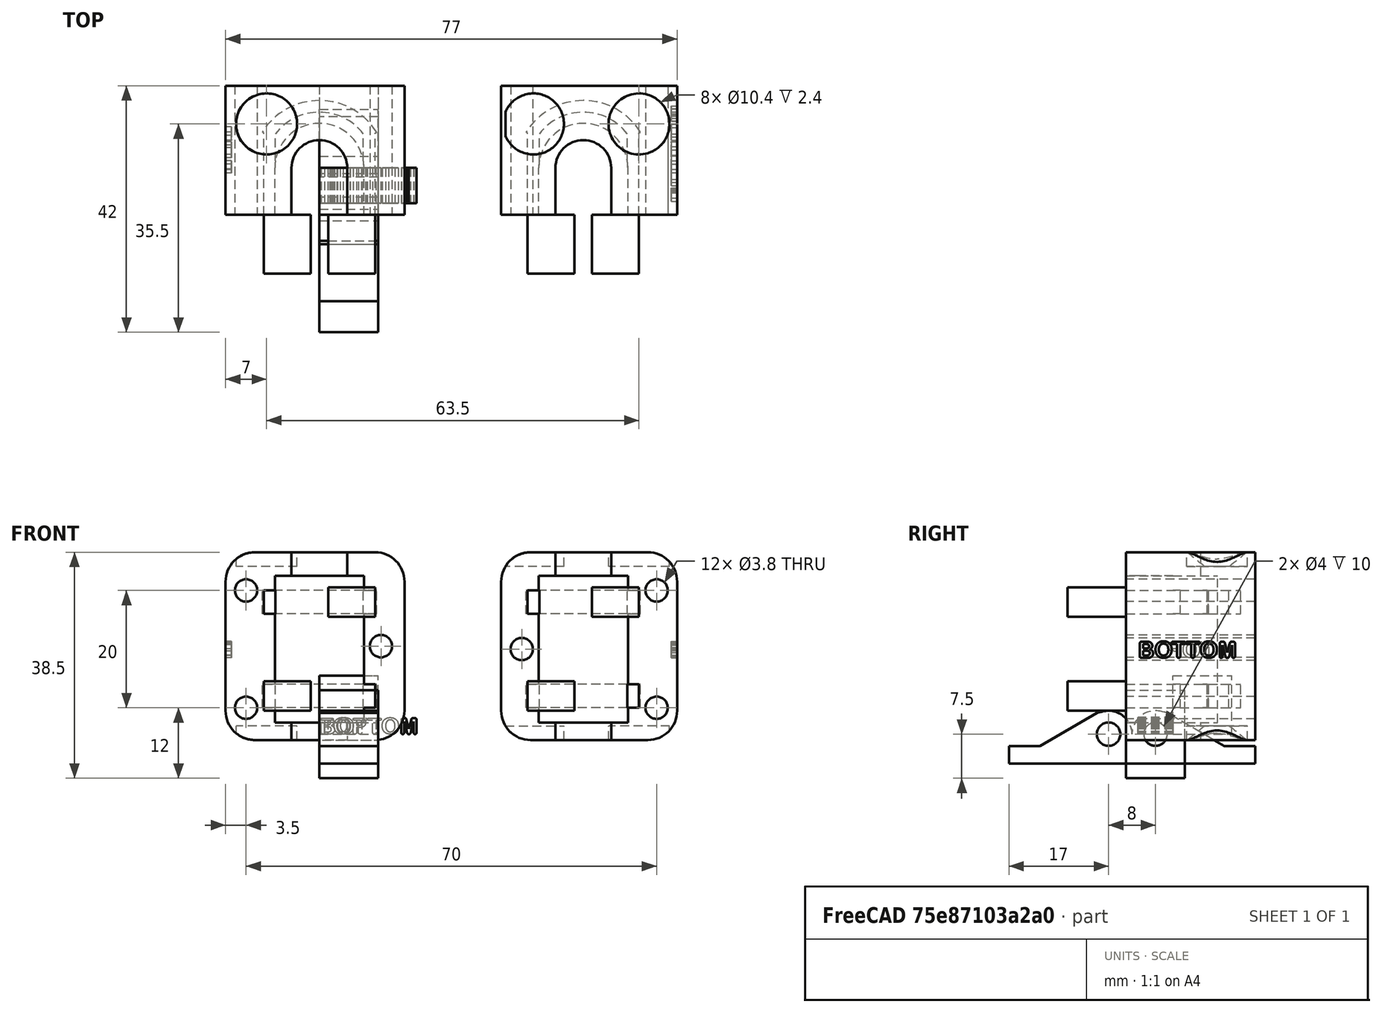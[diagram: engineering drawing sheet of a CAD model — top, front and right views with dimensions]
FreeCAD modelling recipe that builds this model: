
FCSTD DOCUMENT  (FreeCAD 0.16R6712 (Git))
Label: ParkingNozzleSlider
License: All rights reserved
LicenseURL: http://en.wikipedia.org/wiki/All_rights_reserved
objects: Part::Cylinder×51, Part::Box×26, Part::MultiFuse×26, Part::Cut×17, Part::Feature×3, Part::Part2DObjectPython×2, Part::Extrusion×2
note: 127 computed .brp shape members not serialized (recipe doc carries the construction recipe); baked Part::Feature solids carry a one-line shape summary decoded from their .brp

FEATURE [Part::Box] Box  label="Würfel"
  Height = 10
  Length = 10
  Width = 10
FEATURE [Part::Cylinder] Cylinder001  label="RJ4JP"
  Angle = 360
  Height = 25
  Placement = pos=(0,0,-0.5) rot=(0,0,1;0rad)
  Radius = 7.6
FEATURE [Part::Cylinder] Cylinder002  label="LinearStange8mm"
  Angle = 360
  Height = 44
  Placement = pos=(0,0,-10) rot=(0,0,1;0rad)
  Radius = 4.5
FEATURE [Part::Cylinder] Cylinder003  label="LinearSpacer9mm"
  Angle = 360
  Height = 34
  Placement = pos=(0,0,-5) rot=(0,0,1;0rad)
  Radius = 4.75
FEATURE [Part::MultiFuse] Fusion  label="GleitlagerAusspahrung"
  Shapes = -> [Cylinder001,Cylinder003,Cylinder002]
FEATURE [Part::Cylinder] Cylinder004  label="Zylinder001"
  Angle = 116
  Height = 4
  Placement = pos=(0,0,0) rot=(0,0,1;0.558505rad)
  Radius = 11.5
FEATURE [Part::Cylinder] Cylinder005  label="Zylinder002"
  Angle = 116
  Height = 4
  Placement = pos=(0,0,0) rot=(0,0,1;0.558505rad)
  Radius = 9.5
FEATURE [Part::Cut] Cut
  Base = -> Cylinder004
  Tool = -> Cylinder005
FEATURE [Part::Box] Box001  label="Würfel001"
  Height = 4
  Length = 2
  Placement = pos=(-9.5,-11,0) rot=(0,0,1;0rad)
  Width = 17
FEATURE [Part::Box] Box002  label="Würfel002"
  Height = 4
  Length = 2
  Placement = pos=(7.5,-11,0) rot=(0,0,1;0rad)
  Width = 17
FEATURE [Part::MultiFuse] Fusion001  label="KabelbinderAusspahrung002"
  Placement = pos=(0,0,18) rot=(0,0,1;0rad)
  Shapes = -> [Cut,Box002,Box001]
FEATURE [Part::Box] Box009  label="Würfel009"
  Height = 15
  Length = 10
  Placement = pos=(0,-8,-7.5) rot=(0,0,1;0rad)
  Width = 10
FEATURE [Part::Cylinder] Cylinder014  label="Zylinder008"
  Angle = 116
  Height = 4
  Placement = pos=(0,0,0) rot=(0,0,1;0.558505rad)
  Radius = 11.5
FEATURE [Part::Cylinder] Cylinder015  label="Zylinder009"
  Angle = 116
  Height = 4
  Placement = pos=(0,0,0) rot=(0,0,1;0.558505rad)
  Radius = 9.5
FEATURE [Part::Cut] Cut004
  Base = -> Cylinder014
  Tool = -> Cylinder015
FEATURE [Part::Box] Box010  label="Würfel010"
  Height = 4
  Length = 2
  Placement = pos=(-9.5,-11,0) rot=(0,0,1;0rad)
  Width = 17
FEATURE [Part::Box] Box011  label="Würfel011"
  Height = 4
  Length = 2
  Placement = pos=(7.5,-11,0) rot=(0,0,1;0rad)
  Width = 17
FEATURE [Part::MultiFuse] Fusion008  label="KabelbinderAusspahrung005"
  Placement = pos=(0,0,2) rot=(0,0,1;0rad)
  Shapes = -> [Cut004,Box011,Box010]
FEATURE [Part::Box] Box016  label="Block_A"
  Height = 32
  Length = 30.5
  Placement = pos=(-16,-8,-1) rot=(0,0,1;0rad)
  Width = 22
FEATURE [Part::Box] Box017  label="Würfel017"
  Height = 44
  Length = 9.5
  Placement = pos=(-4.75,-11,-10) rot=(0,0,1;0rad)
  Width = 11
FEATURE [Part::Box] Box018  label="Würfel018"
  Height = 25
  Length = 15.2
  Placement = pos=(-7.6,-11,-0.5) rot=(0,0,1;0rad)
  Width = 11
FEATURE [Part::MultiFuse] Fusion014  label="Schacht"
  Shapes = -> [Box017,Box018]
FEATURE [Part::MultiFuse] Fusion015  label="RJ4JP_Cut_Full_A"
  Shapes = -> [Fusion,Fusion001,Fusion008,Fusion014]
FEATURE [Part::Cylinder] Cylinder016  label="RJ4JP001"
  Angle = 360
  Height = 25
  Placement = pos=(0,0,-0.5) rot=(0,0,1;0rad)
  Radius = 7.6
FEATURE [Part::Cylinder] Cylinder017  label="LinearStange8mm001"
  Angle = 360
  Height = 44
  Placement = pos=(0,0,-10) rot=(0,0,1;0rad)
  Radius = 4.5
FEATURE [Part::Cylinder] Cylinder018  label="LinearSpacer9mm001"
  Angle = 360
  Height = 34
  Placement = pos=(0,0,-5) rot=(0,0,1;0rad)
  Radius = 4.75
FEATURE [Part::MultiFuse] Fusion016  label="GleitlagerAusspahrung001"
  Shapes = -> [Cylinder016,Cylinder018,Cylinder017]
FEATURE [Part::Cylinder] Cylinder019  label="Zylinder010"
  Angle = 116
  Height = 4
  Placement = pos=(0,0,0) rot=(0,0,1;0.558505rad)
  Radius = 11.5
FEATURE [Part::Cylinder] Cylinder020  label="Zylinder011"
  Angle = 116
  Height = 4
  Placement = pos=(0,0,0) rot=(0,0,1;0.558505rad)
  Radius = 9.5
FEATURE [Part::Cut] Cut005
  Base = -> Cylinder019
  Tool = -> Cylinder020
FEATURE [Part::Box] Box019  label="Würfel019"
  Height = 4
  Length = 2
  Placement = pos=(-9.5,-11,0) rot=(0,0,1;0rad)
  Width = 17
FEATURE [Part::Box] Box020  label="Würfel020"
  Height = 4
  Length = 2
  Placement = pos=(7.5,-11,0) rot=(0,0,1;0rad)
  Width = 17
FEATURE [Part::MultiFuse] Fusion017  label="KabelbinderAusspahrung006"
  Placement = pos=(0,0,18) rot=(0,0,1;0rad)
  Shapes = -> [Cut005,Box020,Box019]
FEATURE [Part::Cylinder] Cylinder021  label="Zylinder012"
  Angle = 116
  Height = 4
  Placement = pos=(0,0,0) rot=(0,0,1;0.558505rad)
  Radius = 11.5
FEATURE [Part::Cylinder] Cylinder022  label="Zylinder013"
  Angle = 116
  Height = 4
  Placement = pos=(0,0,0) rot=(0,0,1;0.558505rad)
  Radius = 9.5
FEATURE [Part::Cut] Cut006
  Base = -> Cylinder021
  Tool = -> Cylinder022
FEATURE [Part::Box] Box021  label="Würfel021"
  Height = 4
  Length = 2
  Placement = pos=(-9.5,-11,0) rot=(0,0,1;0rad)
  Width = 17
FEATURE [Part::Box] Box022  label="Würfel022"
  Height = 4
  Length = 2
  Placement = pos=(7.5,-11,0) rot=(0,0,1;0rad)
  Width = 17
FEATURE [Part::MultiFuse] Fusion018  label="KabelbinderAusspahrung007"
  Placement = pos=(0,0,2) rot=(0,0,1;0rad)
  Shapes = -> [Cut006,Box022,Box021]
FEATURE [Part::Box] Box023  label="Würfel023"
  Height = 44
  Length = 9.5
  Placement = pos=(-4.75,-11,-10) rot=(0,0,1;0rad)
  Width = 11
FEATURE [Part::Box] Box024  label="Würfel024"
  Height = 25
  Length = 15.2
  Placement = pos=(-7.6,-11,-0.5) rot=(0,0,1;0rad)
  Width = 11
FEATURE [Part::MultiFuse] Fusion019  label="Schacht001"
  Shapes = -> [Box023,Box024]
FEATURE [Part::MultiFuse] Fusion020  label="RJ4JP_Cut_Full_B"
  Placement = pos=(45,0,0) rot=(0,0,1;0rad)
  Shapes = -> [Fusion016,Fusion017,Fusion018,Fusion019]
FEATURE [Part::MultiFuse] Fusion021  label="X_RJ4JP_Cut"
  Placement = pos=(0,0,2.5) rot=(0,0,1;0rad)
  Shapes = -> [Fusion015,Fusion020]
FEATURE [Part::Box] Box025  label="Block_B"
  Height = 32
  Length = 30
  Placement = pos=(31,-8,-1) rot=(0,0,1;0rad)
  Width = 22
FEATURE [Part::MultiFuse] Fusion022  label="GleitBlock"
  Shapes = -> [Box016,Box025]
FEATURE [Part::Cut] Cut007  label="GleitBloecke"
  Base = -> Fusion022
  Tool = -> Fusion021
FEATURE [Part::Cylinder] Cylinder025  label="Zylinder016"
  Angle = 360
  Height = 10
  Radius = 2
FEATURE [Part::Cylinder] Cylinder026  label="Zylinder017"
  Angle = 360
  Height = 10
  Radius = 4
FEATURE [Part::Cut] Cut009
  Base = -> Cylinder026
  Placement = pos=(0,-11,0) rot=(0,0,1;0rad)
  Tool = -> Cylinder025
FEATURE [Part::Box] Box028  label="Würfel027"
  Height = 10
  Length = 3
  Placement = pos=(2,-28,0) rot=(0,0,1;0rad)
  Width = 22
FEATURE [Part::Box] Box029  label="Würfel028"
  Height = 10
  Length = 1
  Placement = pos=(3.9,-26,0) rot=(0,0,1;0.523599rad)
  Width = 15
FEATURE [Part::Box] Box030  label="Würfel029"
  Height = 10
  Length = 3.3
  Placement = pos=(2,-21.5,0) rot=(0,0,1;0.523599rad)
  Width = 8
FEATURE [Part::Cylinder] Cylinder027  label="Zylinder018"
  Angle = 360
  Height = 10
  Placement = pos=(2,-15,0) rot=(0,0,1;0rad)
  Radius = 2
FEATURE [Part::Cylinder] Cylinder028  label="Zylinder019"
  Angle = 360
  Height = 10
  Placement = pos=(-2.73,-12.5,0) rot=(0,0,1;0rad)
  Radius = 1
FEATURE [Part::MultiFuse] Fusion023
  Shapes = -> [Cut009,Cylinder027,Cylinder028,Box028,Box029,Box030]
FEATURE [Part::Cylinder] Cylinder029  label="Zylinder020"
  Angle = 360
  Height = 10
  Radius = 2
FEATURE [Part::Cylinder] Cylinder030  label="Zylinder021"
  Angle = 360
  Height = 10
  Radius = 4
FEATURE [Part::Cut] Cut010
  Base = -> Cylinder030
  Placement = pos=(0,-11,0) rot=(0,0,1;0rad)
  Tool = -> Cylinder029
FEATURE [Part::Box] Box031  label="Würfel030"
  Height = 10
  Length = 3
  Placement = pos=(2,-28,0) rot=(0,0,1;0rad)
  Width = 20
FEATURE [Part::Box] Box032  label="Würfel031"
  Height = 10
  Length = 1
  Placement = pos=(3.9,-26,0) rot=(0,0,1;0.523599rad)
  Width = 15
FEATURE [Part::Box] Box033  label="Würfel032"
  Height = 10
  Length = 3.3
  Placement = pos=(2,-21.5,0) rot=(0,0,1;0.523599rad)
  Width = 8
FEATURE [Part::Cylinder] Cylinder031  label="Zylinder022"
  Angle = 360
  Height = 10
  Placement = pos=(2,-15,0) rot=(0,0,1;0rad)
  Radius = 2
FEATURE [Part::Cylinder] Cylinder032  label="Zylinder023"
  Angle = 360
  Height = 10
  Placement = pos=(-2.73,-12.5,0) rot=(0,0,1;0rad)
  Radius = 1
FEATURE [Part::MultiFuse] Fusion024
  Placement = pos=(0,-14,10) rot=(1,0,0;3.14159rad)
  Shapes = -> [Cut010,Cylinder031,Cylinder032,Box031,Box032,Box033]
FEATURE [Part::MultiFuse] Fusion025
  Shapes = -> [Fusion023,Fusion024]
FEATURE [Part::Cylinder] Cylinder033  label="Zylinder024"
  Angle = 360
  Height = 10
  Placement = pos=(2,-7,0) rot=(0,0,1;0rad)
  Radius = 2
FEATURE [Part::MultiFuse] Fusion026
  Placement = pos=(0,0,0) rot=(0,1,0;1.5708rad)
  Shapes = -> [Fusion025,Cylinder033]
FEATURE [Part::Cylinder] Cylinder034  label="Zylinder025"
  Angle = 360
  Height = 26
  Placement = pos=(-13,16,4.5) rot=(1,0,0;1.5708rad)
  Radius = 1.9
FEATURE [Part::Cylinder] Cylinder035  label="Zylinder026"
  Angle = 360
  Height = 26
  Placement = pos=(-13,16,24.5) rot=(1,0,0;1.5708rad)
  Radius = 1.9
FEATURE [Part::Cylinder] Cylinder036  label="Zylinder027"
  Angle = 360
  Height = 26
  Placement = pos=(10.5,16,15) rot=(1,0,0;1.5708rad)
  Radius = 1.9
FEATURE [Part::MultiFuse] Fusion026003
  Placement = pos=(0.5,0,0) rot=(0,0,1;0rad)
  Shapes = -> [Cylinder034,Cylinder035]
FEATURE [Part::Cylinder] Cylinder037  label="Zylinder028"
  Angle = 360
  Height = 26
  Placement = pos=(-13,16,4.5) rot=(1,0,0;1.5708rad)
  Radius = 1.9
FEATURE [Part::Cylinder] Cylinder038  label="Zylinder029"
  Angle = 360
  Height = 26
  Placement = pos=(-13,16,24.5) rot=(1,0,0;1.5708rad)
  Radius = 1.9
FEATURE [Part::MultiFuse] Fusion026004
  Placement = pos=(70.5,0,0) rot=(0,0,1;0rad)
  Shapes = -> [Cylinder037,Cylinder038]
FEATURE [Part::Cylinder] Cylinder039  label="Zylinder030"
  Angle = 360
  Height = 26
  Placement = pos=(34.5,16,14.5) rot=(1,0,0;1.5708rad)
  Radius = 1.9
FEATURE [Part::MultiFuse] Fusion026005  label="Bohrung"
  Shapes = -> [Cylinder036,Fusion026003,Fusion026004,Cylinder039]
FEATURE [Part::Part2DObjectPython] ShapeString  # Draft 2D object (typed FeaturePython)
  FontFile = <path>
  Size = 3
  String = TOP
  Tracking = 4
FEATURE [Part::Extrusion] Extrude
  Base = -> ShapeString
  Dir = (0,0,6)
  Placement = pos=(0,0,0) rot=(1,0,0;1.5708rad)
  Solid = false
FEATURE [Part::Part2DObjectPython] ShapeString001  # Draft 2D object (typed FeaturePython)
  FontFile = <path>
  Size = 3
  String = BOTTOM
  Tracking = 4
FEATURE [Part::Extrusion] Extrude001
  Base = -> ShapeString001
  Dir = (0,0,6)
  Placement = pos=(0,0,0) rot=(1,0,0;1.5708rad)
  Solid = false
FEATURE [Part::Feature] Extrude002
  Placement = pos=(-15,7,13) rot=(0,0,-1;1.5708rad)
  shape: bbox 6 x 7.877 x 2.835 mm, 76 faces, 3 solids (baked)
FEATURE [Part::Feature] Extrude001001  label="Extrude003"
  Placement = pos=(60,-6,13) rot=(0,0,1;1.5708rad)
  shape: bbox 6 x 16.23 x 2.835 mm, 171 faces, 6 solids (baked)
FEATURE [Part::MultiFuse] Fusion026006  label="Label"
  Shapes = -> [Extrude002,Extrude001001]
FEATURE [Part::Cut] Cut011002  label="Bloecke"
  Base = -> Cut007
  Tool = -> Fusion026006
FEATURE [Part::Cylinder] Cylinder041  label="Zylinder032"
  Angle = 360
  Height = 2.4
  Placement = pos=(-9,0,0) rot=(0,0,1;0rad)
  Radius = 5.2
FEATURE [Part::Cylinder] Cylinder042  label="Zylinder033"
  Angle = 360
  Height = 2.4
  Placement = pos=(54.5,0,0) rot=(0,0,1;0rad)
  Radius = 5.2
FEATURE [Part::Cylinder] Cylinder043  label="Zylinder034"
  Angle = 360
  Height = 2.4
  Placement = pos=(36.5,0,0) rot=(0,0,1;0rad)
  Radius = 5.2
FEATURE [Part::MultiFuse] Fusion026009  label="MagnetsLeft"
  Placement = pos=(0,7.5,28.6) rot=(0,0,1;0rad)
  Shapes = -> [Cylinder041,Cylinder043,Cylinder042]
FEATURE [Part::Cylinder] Cylinder044  label="Zylinder035"
  Angle = 360
  Height = 2.4
  Placement = pos=(-9,0,0) rot=(0,0,1;0rad)
  Radius = 5.2
FEATURE [Part::Cylinder] Cylinder045  label="Zylinder036"
  Angle = 360
  Height = 2.4
  Placement = pos=(54.5,0,0) rot=(0,0,1;0rad)
  Radius = 5.2
FEATURE [Part::Cylinder] Cylinder046  label="Zylinder037"
  Angle = 360
  Height = 2.4
  Placement = pos=(36.5,0,0) rot=(0,0,1;0rad)
  Radius = 5.2
FEATURE [Part::MultiFuse] Fusion026010  label="MagnetsRight"
  Placement = pos=(0,7.5,-1) rot=(0,0,1;0rad)
  Shapes = -> [Cylinder044,Cylinder046,Cylinder045]
FEATURE [Part::MultiFuse] Fusion026011  label="Magnets"
  Shapes = -> [Fusion026009,Fusion026010]
FEATURE [Part::Cylinder] Cylinder047  label="Zylinder038"
  Angle = 90
  Height = 40
  Placement = pos=(33,25,29) rot=(1,0,0;1.5708rad)
  Radius = 8
FEATURE [Part::Cylinder] Cylinder048  label="Zylinder039"
  Angle = 90
  Height = 40
  Placement = pos=(33,25,29) rot=(1,0,0;1.5708rad)
  Radius = 5
FEATURE [Part::Cut] Cut011004002
  Base = -> Cylinder047
  Placement = pos=(65,0,-7) rot=(0,-1,0;1.5708rad)
  Tool = -> Cylinder048
FEATURE [Part::Cylinder] Cylinder049  label="Zylinder040"
  Angle = 90
  Height = 40
  Placement = pos=(33,25,29) rot=(1,0,0;1.5708rad)
  Radius = 8
FEATURE [Part::Cylinder] Cylinder050  label="Zylinder041"
  Angle = 90
  Height = 40
  Placement = pos=(33,25,29) rot=(1,0,0;1.5708rad)
  Radius = 5
FEATURE [Part::Cut] Cut011004003
  Base = -> Cylinder049
  Placement = pos=(69,0,33) rot=(0,1,0;3.14159rad)
  Tool = -> Cylinder050
FEATURE [Part::Cylinder] Cylinder051  label="Zylinder042"
  Angle = 90
  Height = 40
  Placement = pos=(33,25,29) rot=(1,0,0;1.5708rad)
  Radius = 8
FEATURE [Part::Cylinder] Cylinder052  label="Zylinder043"
  Angle = 90
  Height = 40
  Placement = pos=(33,25,29) rot=(1,0,0;1.5708rad)
  Radius = 5
FEATURE [Part::Cut] Cut011004004
  Base = -> Cylinder051
  Placement = pos=(18,0,-7) rot=(0,-1,0;1.5708rad)
  Tool = -> Cylinder052
FEATURE [Part::Cylinder] Cylinder053  label="Zylinder044"
  Angle = 90
  Height = 40
  Placement = pos=(33,25,29) rot=(1,0,0;1.5708rad)
  Radius = 8
FEATURE [Part::Cylinder] Cylinder054  label="Zylinder045"
  Angle = 90
  Height = 40
  Placement = pos=(33,25,29) rot=(1,0,0;1.5708rad)
  Radius = 5
FEATURE [Part::Cut] Cut011004005
  Base = -> Cylinder053
  Placement = pos=(22,0,33) rot=(0,1,0;3.14159rad)
  Tool = -> Cylinder054
FEATURE [Part::Cylinder] Cylinder055  label="Zylinder046"
  Angle = 90
  Height = 40
  Placement = pos=(33,25,29) rot=(1,0,0;1.5708rad)
  Radius = 8
FEATURE [Part::Cylinder] Cylinder056  label="Zylinder047"
  Angle = 90
  Height = 40
  Placement = pos=(33,25,29) rot=(1,0,0;1.5708rad)
  Radius = 5
FEATURE [Part::Cut] Cut011004006
  Base = -> Cylinder055
  Placement = pos=(23,0,-3) rot=(0,0,1;0rad)
  Tool = -> Cylinder056
FEATURE [Part::Cylinder] Cylinder057  label="Zylinder048"
  Angle = 90
  Height = 40
  Placement = pos=(33,25,29) rot=(1,0,0;1.5708rad)
  Radius = 8
FEATURE [Part::Cylinder] Cylinder058  label="Zylinder049"
  Angle = 90
  Height = 40
  Placement = pos=(33,25,29) rot=(1,0,0;1.5708rad)
  Radius = 5
FEATURE [Part::Cut] Cut011004007
  Base = -> Cylinder057
  Placement = pos=(-19.5,0,37) rot=(0,1,0;1.5708rad)
  Tool = -> Cylinder058
FEATURE [Part::Cylinder] Cylinder059  label="Zylinder050"
  Angle = 90
  Height = 40
  Placement = pos=(33,25,29) rot=(1,0,0;1.5708rad)
  Radius = 8
FEATURE [Part::Cylinder] Cylinder060  label="Zylinder051"
  Angle = 90
  Height = 40
  Placement = pos=(33,25,29) rot=(1,0,0;1.5708rad)
  Radius = 5
FEATURE [Part::Cut] Cut011004008
  Base = -> Cylinder059
  Placement = pos=(27,0,37) rot=(0,1,0;1.5708rad)
  Tool = -> Cylinder060
FEATURE [Part::Cylinder] Cylinder061  label="Zylinder052"
  Angle = 90
  Height = 40
  Placement = pos=(33,25,29) rot=(1,0,0;1.5708rad)
  Radius = 8
FEATURE [Part::Cylinder] Cylinder062  label="Zylinder053"
  Angle = 90
  Height = 40
  Placement = pos=(33,25,29) rot=(1,0,0;1.5708rad)
  Radius = 5
FEATURE [Part::Cut] Cut011004009
  Base = -> Cylinder061
  Placement = pos=(-23.5,0,-3) rot=(0,0,1;0rad)
  Tool = -> Cylinder062
FEATURE [Part::MultiFuse] Fusion026012  label="RoundEdges"
  Shapes = -> [Cut011004002,Cut011004003,Cut011004009,Cut011004008,Cut011004006,Cut011004007,Cut011004004,Cut011004005]
FEATURE [Part::MultiFuse] Fusion026014  label="To_Cut"
  Shapes = -> [Fusion026012,Fusion026011,Fusion026005]
FEATURE [Part::Cut] Cut011004010  label="NozzleSliderMag10"
  Base = -> Cut011002
  Tool = -> Fusion026014
FEATURE [Part::Box] Box034  label="Würfel033"
  Height = 5
  Length = 8
  Placement = pos=(-9.5,-18,4) rot=(0,0,1;0rad)
  Width = 10
FEATURE [Part::Box] Box035  label="Würfel034"
  Height = 5
  Length = 8
  Placement = pos=(35.5,-18,4) rot=(0,0,1;0rad)
  Width = 10
FEATURE [Part::Box] Box036  label="Würfel035"
  Height = 5
  Length = 8
  Placement = pos=(1.5,-18,20) rot=(0,0,1;0rad)
  Width = 10
FEATURE [Part::Box] Box037  label="Würfel036"
  Height = 5
  Length = 8
  Placement = pos=(46.5,-18,20) rot=(0,0,1;0rad)
  Width = 10
FEATURE [Part::MultiFuse] Fusion026015  label="SripperHoles"
  Shapes = -> [Box034,Box037,Box035,Box036]
FEATURE [Part::Feature] Cut011004010001  label="NozzleSliderMag10_export"
  shape: bbox 77 x 22 x 32 mm, 354 faces, 2 solids (baked)
note: 2 file-system paths scrubbed to <path> (originals preserved in the JSON sidecar)
